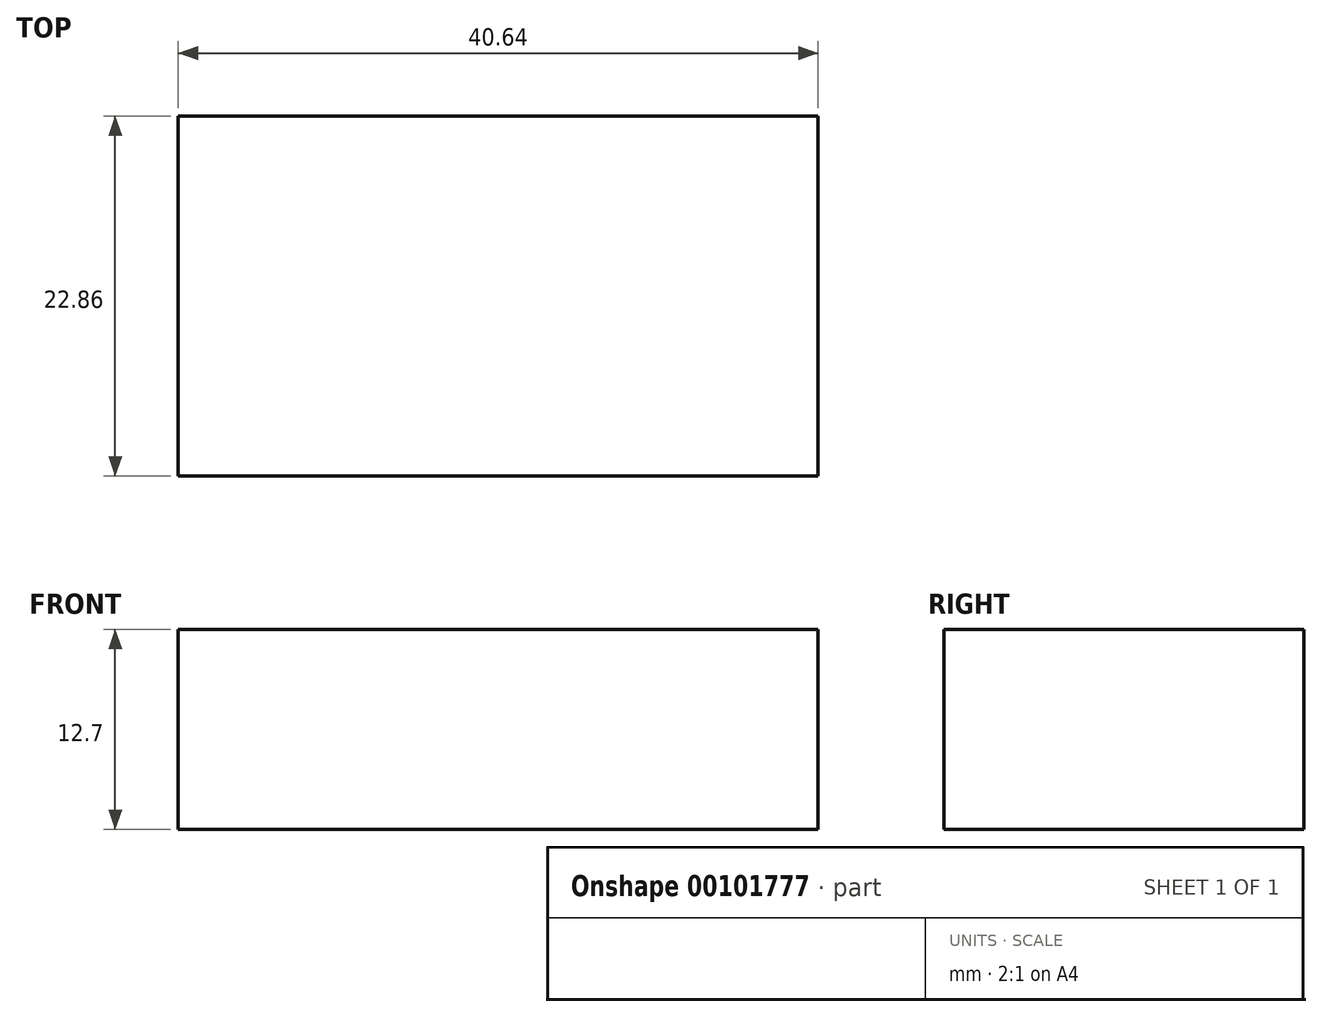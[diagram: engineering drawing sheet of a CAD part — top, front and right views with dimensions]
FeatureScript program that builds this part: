
annotation { "Feature Type Name" : "Feature", "Feature Type Description" : "" }
export const myFeature = defineFeature(function(context is Context, id is Id, definition is map)
    precondition{}
    {
        {
            var Q0;
            Q0=qCreatedBy(makeId("Front.planeOp"),FACE);
            var sketch = newSketch(context, id + "F0", { "sketchPlane" : qUnion([Q0])});
            skLineSegment(sketch, "E0.bottom", {"start": v(-35.76, 9.87) * mm, "end": v(4.88, 9.87) * mm});
            skLineSegment(sketch, "E0.top", {"start": v(-35.76, -2.83) * mm, "end": v(4.88, -2.83) * mm});
            skLineSegment(sketch, "E0.left", {"start": v(-35.76, 9.87) * mm, "end": v(-35.76, -2.83) * mm});
            skLineSegment(sketch, "E0.right", {"start": v(4.88, 9.87) * mm, "end": v(4.88, -2.83) * mm});
            skSolve(sketch);
        }
        {
            var Q0;
            Q0=makeQuery(id+"F0.imprint","IMPRINT",FACE,{"disambiguationData":[TD([[makeQuery(id+"F0.imprint","IMPRINT",EDGE,{"derivedFrom":sQuery(id+"F0.wireOp",EDGE,"E0.bottom")}),-1.0]])]});
            extrude(context, id + "F1", {"entities" : qUnion([Q0]), "depth" : 22.86 * mm});
        }
    });
